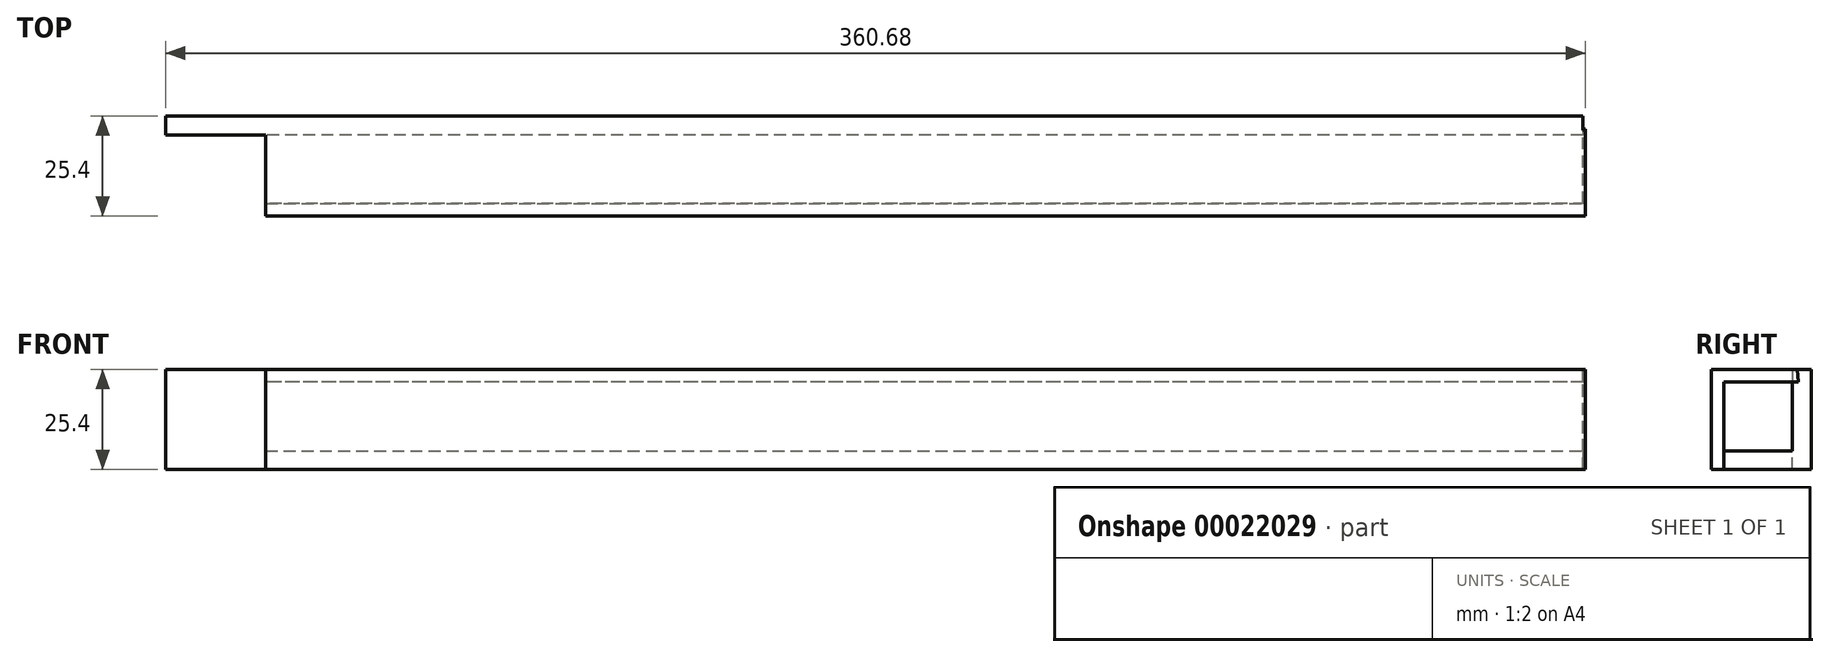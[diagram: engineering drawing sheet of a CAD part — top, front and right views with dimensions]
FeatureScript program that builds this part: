
annotation { "Feature Type Name" : "Feature", "Feature Type Description" : "" }
export const myFeature = defineFeature(function(context is Context, id is Id, definition is map)
    precondition{}
    {
        {
            var Q0;
            Q0=qCreatedBy(makeId("Right.planeOp"),FACE);
            var sketch = newSketch(context, id + "F0", { "sketchPlane" : qUnion([Q0])});
            skLineSegment(sketch, "E0.top", {"start": v(-25.23, 14.25) * mm, "end": v(0.17, 14.25) * mm});
            skLineSegment(sketch, "E0.left", {"start": v(-25.23, 19.02) * mm, "end": v(-25.23, 14.25) * mm});
            skLineSegment(sketch, "E1.top", {"start": v(-4.6, 39.65) * mm, "end": v(0.17, 39.65) * mm});
            skLineSegment(sketch, "E1.left", {"start": v(-4.6, 19.02) * mm, "end": v(-4.6, 39.65) * mm});
            skLineSegment(sketch, "E1.right", {"start": v(0.17, 14.25) * mm, "end": v(0.17, 39.65) * mm});
            skLineSegment(sketch, "E2", {"start": v(-25.23, 19.02) * mm, "end": v(-4.6, 19.02) * mm});
            skSolve(sketch);
        }
        {
            var Q0;
            Q0 = qSketchRegion(id + "F0", true);
            extrude(context, id + "F1", {"entities" : qUnion([Q0]), "depth" : 360 * mm});
        }
        {
            var Q0;
            Q0=makeQuery(id+"F1.opExtrude","SWEPT_FACE",FACE,{"disambiguationData":[OSD([sQuery(id+"F0.wireOp",EDGE,"E2")])]});
            var sketch = newSketch(context, id + "F2", { "sketchPlane" : qUnion([Q0])});
            skLineSegment(sketch, "E3.bottom", {"start": v(0, -4.6) * mm, "end": v(25.4, -4.6) * mm});
            skLineSegment(sketch, "E3.top", {"start": v(0, -25.23) * mm, "end": v(25.4, -25.23) * mm});
            skLineSegment(sketch, "E3.left", {"start": v(0, -4.6) * mm, "end": v(0, -25.23) * mm});
            skLineSegment(sketch, "E3.right", {"start": v(25.4, -4.6) * mm, "end": v(25.4, -25.23) * mm});
            skLineSegment(sketch, "E4.bottom", {"start": v(360, -4.6) * mm, "end": v(334.6, -4.6) * mm});
            skLineSegment(sketch, "E4.top", {"start": v(360, -25.23) * mm, "end": v(334.6, -25.23) * mm});
            skLineSegment(sketch, "E4.left", {"start": v(360, -4.6) * mm, "end": v(360, -25.23) * mm});
            skLineSegment(sketch, "E4.right", {"start": v(334.6, -4.6) * mm, "end": v(334.6, -25.23) * mm});
            skSolve(sketch);
        }
        {
            var Q0;
            Q0=makeQuery(id+"F2.imprint","IMPRINT",FACE,{"disambiguationData":[TD([[makeQuery(id+"F2.imprint","IMPRINT",EDGE,{"derivedFrom":sQuery(id+"F2.wireOp",EDGE,"E3.bottom")}),1.0]])]});
            extrude(context, id + "F3", {"entities" : qUnion([Q0]), "operationType" : NewBodyOperationType.REMOVE, "oppositeDirection" : true, "depth" : 25.4 * mm});
        }
        {
            var Q0;
            Q0=makeQuery(id+"F3.boolean.opBoolean","COPY",FACE,{"derivedFrom":makeQuery(id+"F3.opExtrude","SWEPT_FACE",FACE,{"disambiguationData":[OSD([sQuery(id+"F2.wireOp",EDGE,"E3.right")])]})});
            var sketch = newSketch(context, id + "F4", { "sketchPlane" : qUnion([Q0])});
            skLineSegment(sketch, "E5", {"start": v(25.23, 14.25) * mm, "end": v(25.23, 39.65) * mm});
            skLineSegment(sketch, "E6", {"start": v(25.23, 14.25) * mm, "end": v(22.06, 14.25) * mm});
            skLineSegment(sketch, "E7", {"start": v(22.06, 14.25) * mm, "end": v(22.06, 39.65) * mm});
            skLineSegment(sketch, "E8", {"start": v(25.23, 39.65) * mm, "end": v(3.4, 39.65) * mm});
            skLineSegment(sketch, "E9", {"start": v(25.23, 39.65) * mm, "end": v(25.23, 36.48) * mm});
            skLineSegment(sketch, "E10", {"start": v(25.23, 36.48) * mm, "end": v(3.12, 36.48) * mm});
            skLineSegment(sketch, "E11", {"start": v(3.4, 39.65) * mm, "end": v(3.12, 36.48) * mm});
            skSolve(sketch);
        }
        {
            var Q0;
            Q0 = qSketchRegion(id + "F4", true);
            extrude(context, id + "F5", {"entities" : qUnion([Q0]), "operationType" : NewBodyOperationType.ADD, "oppositeDirection" : true, "depth" : 335.28 * mm});
        }
    });
